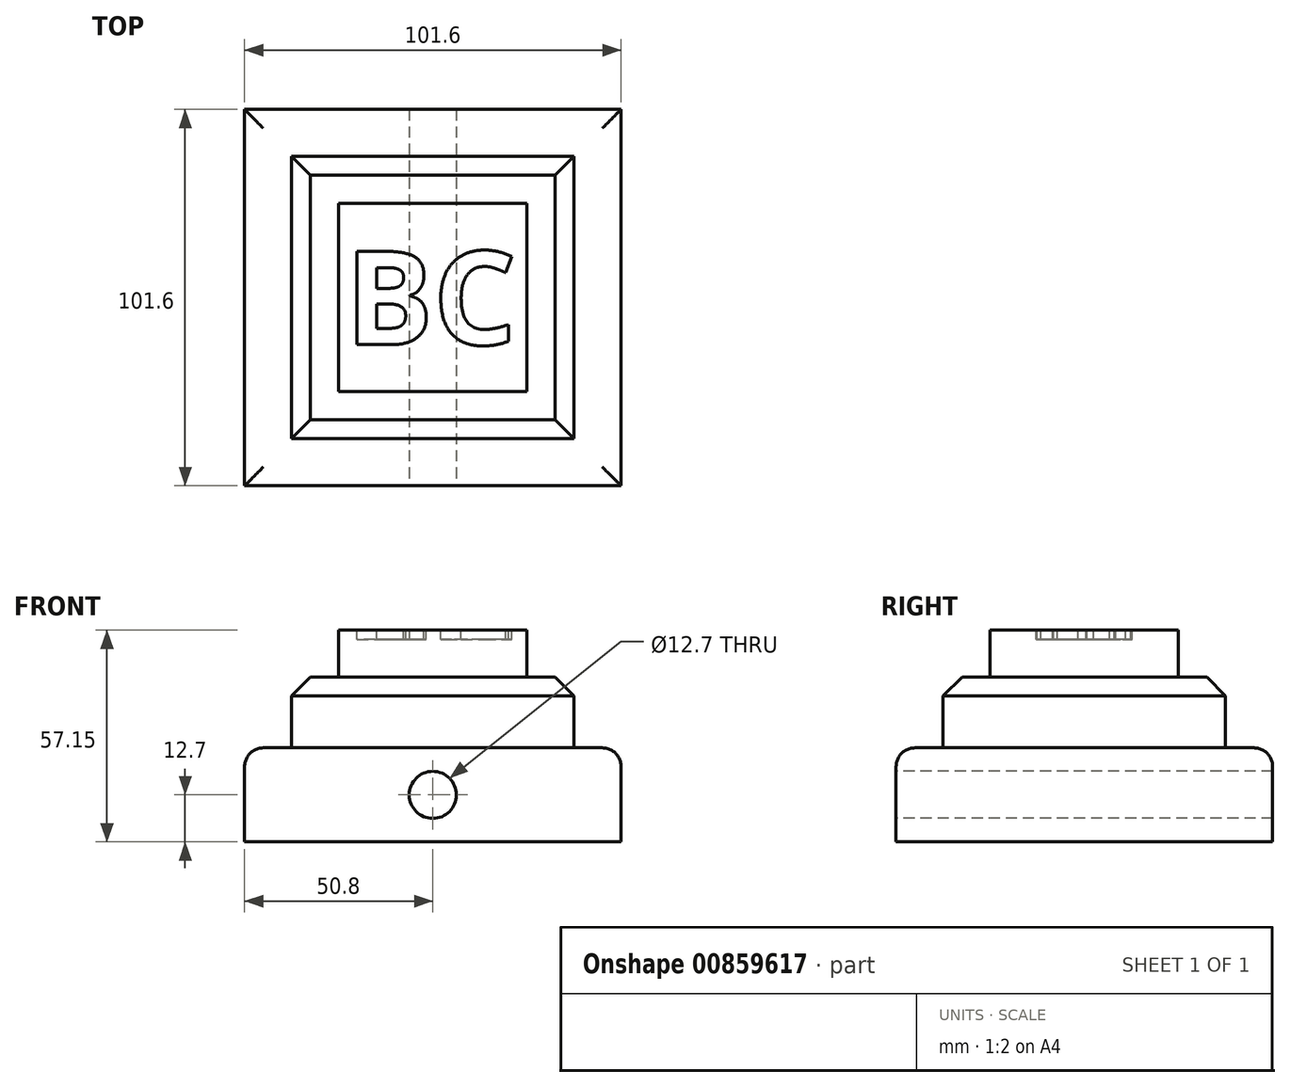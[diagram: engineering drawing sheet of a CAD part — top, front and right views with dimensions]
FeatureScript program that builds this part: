
annotation { "Feature Type Name" : "Feature", "Feature Type Description" : "" }
export const myFeature = defineFeature(function(context is Context, id is Id, definition is map)
    precondition{}
    {
        {
            var Q0;
            Q0=qCreatedBy(makeId("Top.planeOp"),FACE);
            var sketch = newSketch(context, id + "F0", { "sketchPlane" : qUnion([Q0])});
            skLineSegment(sketch, "E0.bottom", {"start": v(0, 0) * mm, "end": v(101.6, 0) * mm});
            skLineSegment(sketch, "E0.top", {"start": v(0, 101.6) * mm, "end": v(101.6, 101.6) * mm});
            skLineSegment(sketch, "E0.left", {"start": v(0, 0) * mm, "end": v(0, 101.6) * mm});
            skLineSegment(sketch, "E0.right", {"start": v(101.6, 0) * mm, "end": v(101.6, 101.6) * mm});
            skSolve(sketch);
        }
        {
            var Q0;
            Q0=makeQuery(id+"F0.imprint","IMPRINT",FACE,{"disambiguationData":[TD([[makeQuery(id+"F0.imprint","IMPRINT",EDGE,{"derivedFrom":sQuery(id+"F0.wireOp",EDGE,"E0.bottom")}),1.0]])]});
            extrude(context, id + "F1", {"entities" : qUnion([Q0]), "depth" : 25.4 * mm, "offsetDistance" : 25.4 * mm});
        }
        {
            var Q0;
            Q0=makeQuery(id+"F1.opExtrude","CAP_FACE",FACE,{"disambiguationData":[OSD([sQuery(id+"F0.wireOp",EDGE,"E0.bottom"),sQuery(id+"F0.wireOp",EDGE,"E0.top"),sQuery(id+"F0.wireOp",EDGE,"E0.left"),sQuery(id+"F0.wireOp",EDGE,"E0.right")])],"isStart":false});
            var sketch = newSketch(context, id + "F2", { "sketchPlane" : qUnion([Q0])});
            skLineSegment(sketch, "E1.0", {"start": v(88.9, 88.9) * mm, "end": v(12.7, 88.9) * mm});
            skLineSegment(sketch, "E1.1", {"start": v(88.9, 12.7) * mm, "end": v(88.9, 88.9) * mm});
            skLineSegment(sketch, "E1.2", {"start": v(12.7, 12.7) * mm, "end": v(88.9, 12.7) * mm});
            skLineSegment(sketch, "E1.3", {"start": v(12.7, 88.9) * mm, "end": v(12.7, 12.7) * mm});
            skSolve(sketch);
        }
        {
            var Q0;
            Q0=makeQuery(id+"F2.imprint","IMPRINT",FACE,{"disambiguationData":[TD([[makeQuery(id+"F2.imprint","IMPRINT",EDGE,{"derivedFrom":sQuery(id+"F2.wireOp",EDGE,"E1.0")}),1.0]])]});
            extrude(context, id + "F3", {"entities" : qUnion([Q0]), "operationType" : NewBodyOperationType.ADD, "depth" : 19.05 * mm, "offsetDistance" : 25.4 * mm});
        }
        {
            var Q0;
            Q0=makeQuery(id+"F3.opExtrude","CAP_FACE",FACE,{"disambiguationData":[OSD([sQuery(id+"F2.wireOp",EDGE,"E1.0"),sQuery(id+"F2.wireOp",EDGE,"E1.1"),sQuery(id+"F2.wireOp",EDGE,"E1.2"),sQuery(id+"F2.wireOp",EDGE,"E1.3")])],"isStart":false});
            var sketch = newSketch(context, id + "F4", { "sketchPlane" : qUnion([Q0])});
            skLineSegment(sketch, "E2.0", {"start": v(76.2, 76.2) * mm, "end": v(25.4, 76.2) * mm});
            skLineSegment(sketch, "E2.1", {"start": v(76.2, 25.4) * mm, "end": v(76.2, 76.2) * mm});
            skLineSegment(sketch, "E2.2", {"start": v(25.4, 25.4) * mm, "end": v(76.2, 25.4) * mm});
            skLineSegment(sketch, "E2.3", {"start": v(25.4, 76.2) * mm, "end": v(25.4, 25.4) * mm});
            skSolve(sketch);
        }
        {
            var Q0;
            Q0=makeQuery(id+"F4.imprint","IMPRINT",FACE,{"disambiguationData":[TD([[makeQuery(id+"F4.imprint","IMPRINT",EDGE,{"derivedFrom":sQuery(id+"F4.wireOp",EDGE,"E2.0")}),1.0]])]});
            extrude(context, id + "F5", {"entities" : qUnion([Q0]), "operationType" : NewBodyOperationType.ADD, "depth" : 12.7 * mm, "offsetDistance" : 25.4 * mm});
        }
        {
            var Q0;
            Q0=makeQuery(id+"F1.opExtrude","SWEPT_FACE",FACE,{"disambiguationData":[OSD([sQuery(id+"F0.wireOp",EDGE,"E0.bottom")])]});
            var sketch = newSketch(context, id + "F6", { "sketchPlane" : qUnion([Q0])});
            skCircle(sketch, "E3", {"center": v(50.8, 12.7) * mm, "radius": 6.35 * mm});
            skSolve(sketch);
        }
        {
            var Q0;
            Q0=makeQuery(id+"F6.imprint","IMPRINT",FACE,{"disambiguationData":[TD([[makeQuery(id+"F6.imprint","IMPRINT",EDGE,{"derivedFrom":sQuery(id+"F6.wireOp",EDGE,"E3")}),1.0]])]});
            extrude(context, id + "F7", {"entities" : qUnion([Q0]), "operationType" : NewBodyOperationType.REMOVE, "oppositeDirection" : true, "depth" : 181.86 * mm, "offsetDistance" : 25.4 * mm});
        }
        {
            var Q0;
            Q0=makeQuery(id+"F1.opExtrude","CAP_EDGE",EDGE,{"disambiguationData":[OSD([sQuery(id+"F0.wireOp",EDGE,"E0.right")])],"isStart":false});
            var Q1;
            Q1=makeQuery(id+"F1.opExtrude","CAP_EDGE",EDGE,{"disambiguationData":[OSD([sQuery(id+"F0.wireOp",EDGE,"E0.bottom")])],"isStart":false});
            var Q2;
            Q2=makeQuery(id+"F1.opExtrude","CAP_EDGE",EDGE,{"disambiguationData":[OSD([sQuery(id+"F0.wireOp",EDGE,"E0.left")])],"isStart":false});
            var Q3;
            Q3=makeQuery(id+"F1.opExtrude","CAP_EDGE",EDGE,{"disambiguationData":[OSD([sQuery(id+"F0.wireOp",EDGE,"E0.top")])],"isStart":false});
            fillet(context, id + "F8", {"entities" : qUnion([Q0, Q1, Q2, Q3]), "radius" : 5.08 * mm, "tangentPropagation" : true, "allowEdgeOverflow" : false});
        }
        {
            var Q0;
            Q0=makeQuery(id+"F3.opExtrude","CAP_EDGE",EDGE,{"disambiguationData":[OSD([sQuery(id+"F2.wireOp",EDGE,"E1.1")])],"isStart":false});
            var Q1;
            Q1=makeQuery(id+"F3.opExtrude","CAP_EDGE",EDGE,{"disambiguationData":[OSD([sQuery(id+"F2.wireOp",EDGE,"E1.2")])],"isStart":false});
            var Q2;
            Q2=makeQuery(id+"F3.opExtrude","CAP_EDGE",EDGE,{"disambiguationData":[OSD([sQuery(id+"F2.wireOp",EDGE,"E1.0")])],"isStart":false});
            var Q3;
            Q3=makeQuery(id+"F3.opExtrude","CAP_EDGE",EDGE,{"disambiguationData":[OSD([sQuery(id+"F2.wireOp",EDGE,"E1.3")])],"isStart":false});
            chamfer(context, id + "F9", {"entities" : qUnion([Q0, Q1, Q2, Q3]), "width" : 5.08 * mm, "tangentPropagation" : true});
        }
        {
            var Q0;
            Q0=makeQuery(id+"F5.opExtrude","CAP_FACE",FACE,{"disambiguationData":[OSD([sQuery(id+"F4.wireOp",EDGE,"E2.0"),sQuery(id+"F4.wireOp",EDGE,"E2.1"),sQuery(id+"F4.wireOp",EDGE,"E2.2"),sQuery(id+"F4.wireOp",EDGE,"E2.3")])],"isStart":false});
            var sketch = newSketch(context, id + "F10", { "sketchPlane" : qUnion([Q0])});
            skText(sketch, "E4", { "text": "BC", "fontName": "OpenSans-Bold.ttf"});
            const initialGuessF10  = {"E4": [0.02719, 0.0381, 1, 0, 0.0254]};
            skSetInitialGuess(sketch, initialGuessF10);
            skSolve(sketch);
        }
        {
            var Q0;
            Q0 = qSketchRegion(id + "F10", true);
            extrude(context, id + "F11", {"entities" : qUnion([Q0]), "operationType" : NewBodyOperationType.REMOVE, "oppositeDirection" : true, "depth" : 2.54 * mm, "offsetDistance" : 25.4 * mm});
        }
    });
